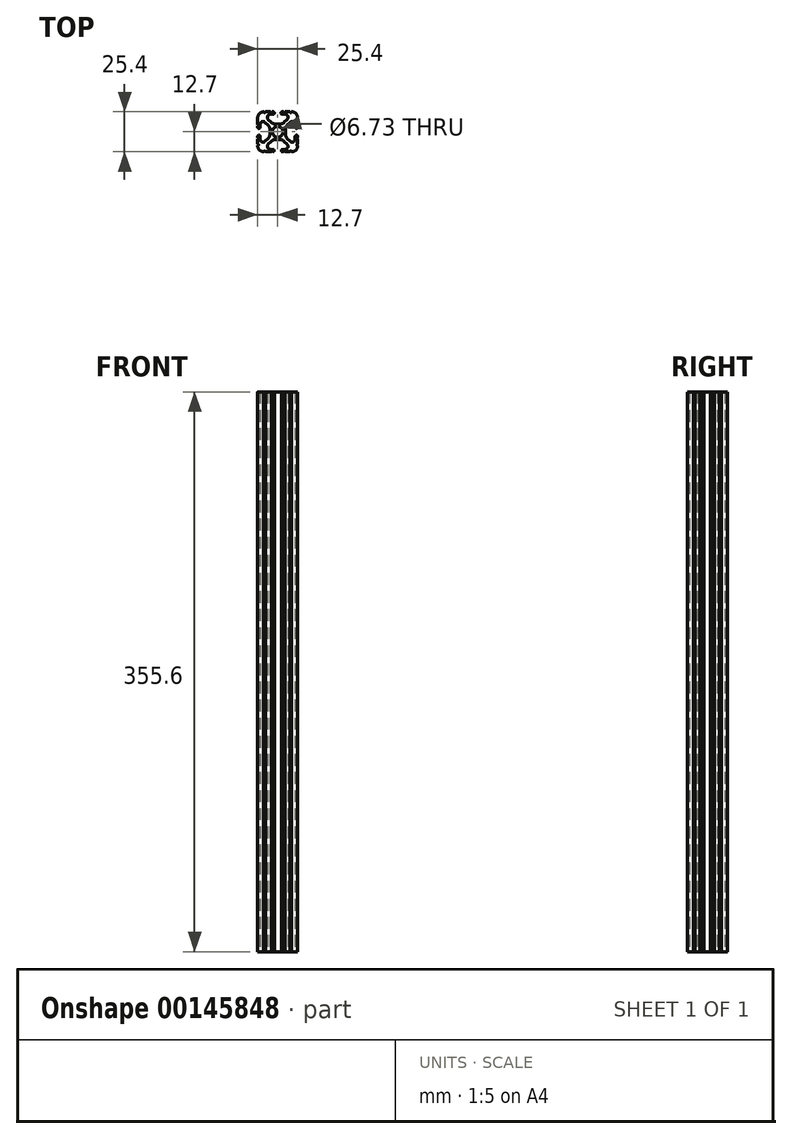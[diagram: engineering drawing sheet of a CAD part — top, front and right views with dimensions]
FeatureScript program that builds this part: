
annotation { "Feature Type Name" : "Feature", "Feature Type Description" : "" }
export const myFeature = defineFeature(function(context is Context, id is Id, definition is map)
    precondition{}
    {
        {
            var Q0;
            Q0=qCreatedBy(makeId("Top.planeOp"),FACE);
            var sketch = newSketch(context, id + "F0", { "sketchPlane" : qUnion([Q0])});
            skCircle(sketch, "E0", {"center": v(-12.7, 12.7) * mm, "radius": 3.36 * mm});
            skLineSegment(sketch, "E1.bottom", {"start": v(-11.24, 17.64) * mm, "end": v(-14.16, 17.64) * mm});
            skLineSegment(sketch, "E1.top", {"start": v(-11.24, 7.76) * mm, "end": v(-14.16, 7.76) * mm});
            skLineSegment(sketch, "E1.left", {"start": v(-7.76, 14.16) * mm, "end": v(-7.76, 11.24) * mm});
            skLineSegment(sketch, "E1.right", {"start": v(-17.64, 14.16) * mm, "end": v(-17.64, 11.24) * mm});
            skPoint(sketch, "E2.visualSharp", {"position": v(-25.4, 25.4) * mm});
            skPoint(sketch, "E3.visualSharp", {"position": v(0, 25.4) * mm});
            skPoint(sketch, "E4.visualSharp", {"position": v(0, 0) * mm});
            skPoint(sketch, "E5.visualSharp", {"position": v(-25.4, 0) * mm});
            skLineSegment(sketch, "E6.0", {"start": v(-18.7, 20.6) * mm, "end": v(-16.85, 18.76) * mm});
            skLineSegment(sketch, "E7.0", {"start": v(-20.6, 18.7) * mm, "end": v(-18.76, 16.85) * mm});
            skPoint(sketch, "E8.orphan", {"position": v(-23.85, 1.55) * mm});
            skPoint(sketch, "E9.orphan", {"position": v(-23.85, 23.85) * mm});
            skPoint(sketch, "E10.orphan", {"position": v(-1.55, 23.85) * mm});
            skPoint(sketch, "E11.orphan", {"position": v(-1.55, 1.55) * mm});
            skLineSegment(sketch, "E12", {"start": v(-8.55, 6.64) * mm, "end": v(-6.7, 4.8) * mm});
            skLineSegment(sketch, "E13.0", {"start": v(-18.7, 4.8) * mm, "end": v(-16.85, 6.64) * mm});
            skLineSegment(sketch, "E14.0", {"start": v(-20.6, 6.7) * mm, "end": v(-18.76, 8.55) * mm});
            skLineSegment(sketch, "E15.0", {"start": v(-8.55, 18.76) * mm, "end": v(-6.7, 20.6) * mm});
            skPoint(sketch, "E16.visualSharp", {"position": v(-23.85, 21.95) * mm});
            skArc(sketch, "E16.filletArc", {"start": v(-20.6, 18.7) * mm, "mid": v(-22.68, 19.1) * mm, "end": v(-23.85, 17.35) * mm});
            skPoint(sketch, "E17.visualSharp", {"position": v(-21.95, 23.85) * mm});
            skArc(sketch, "E17.filletArc", {"start": v(-17.35, 23.85) * mm, "mid": v(-19.1, 22.68) * mm, "end": v(-18.7, 20.6) * mm});
            skPoint(sketch, "E18.visualSharp", {"position": v(-5.34, 23.85) * mm});
            skLineSegment(sketch, "E19", {"start": v(-17.35, 23.85) * mm, "end": v(-15.58, 23.85) * mm});
            skLineSegment(sketch, "E20", {"start": v(-23.85, 17.35) * mm, "end": v(-23.85, 15.62) * mm});
            skLineSegment(sketch, "E21", {"start": v(-8.05, 1.55) * mm, "end": v(-9.78, 1.55) * mm});
            skArc(sketch, "E22.filletArc", {"start": v(-6.7, 20.6) * mm, "mid": v(-6.3, 22.68) * mm, "end": v(-8.05, 23.85) * mm});
            skPoint(sketch, "E23.visualSharp", {"position": v(-1.55, 3.45) * mm});
            skPoint(sketch, "E24.visualSharp", {"position": v(-3.45, 1.55) * mm});
            skArc(sketch, "E24.filletArc", {"start": v(-8.05, 1.55) * mm, "mid": v(-6.3, 2.73) * mm, "end": v(-6.7, 4.8) * mm});
            skArc(sketch, "E25.filletArc", {"start": v(-18.7, 4.8) * mm, "mid": v(-19.1, 2.73) * mm, "end": v(-17.35, 1.55) * mm});
            skArc(sketch, "E26.filletArc", {"start": v(-23.85, 8.05) * mm, "mid": v(-22.68, 6.3) * mm, "end": v(-20.6, 6.7) * mm});
            skLineSegment(sketch, "E27.bottom", {"start": v(-4.9, 0) * mm, "end": v(-8.05, 0) * mm});
            skLineSegment(sketch, "E27.top", {"start": v(-4.92, 25.4) * mm, "end": v(-8.05, 25.4) * mm});
            skLineSegment(sketch, "E27.left", {"start": v(0, 4.9) * mm, "end": v(0, 8.05) * mm});
            skLineSegment(sketch, "E27.right", {"start": v(-25.4, 4.9) * mm, "end": v(-25.4, 8.05) * mm});
            skArc(sketch, "E28.filletArc", {"start": v(-25.4, 3.81) * mm, "mid": v(-24.28, 1.12) * mm, "end": v(-21.59, 0) * mm});
            skArc(sketch, "E29.filletArc", {"start": v(-3.81, 0) * mm, "mid": v(-1.12, 1.12) * mm, "end": v(0, 3.8) * mm});
            skArc(sketch, "E30.filletArc", {"start": v(0, 21.59) * mm, "mid": v(-1.12, 24.28) * mm, "end": v(-3.8, 25.4) * mm});
            skArc(sketch, "E31.filletArc", {"start": v(-21.59, 25.4) * mm, "mid": v(-24.28, 24.28) * mm, "end": v(-25.4, 21.59) * mm});
            skPoint(sketch, "E32.newPointA", {"position": v(-17.64, 7.76) * mm});
            skArc(sketch, "E32.filletArc", {"start": v(-14.16, 7.76) * mm, "mid": v(-15.62, 7.47) * mm, "end": v(-16.85, 6.64) * mm});
            skPoint(sketch, "E33.newPointA", {"position": v(-7.76, 7.76) * mm});
            skArc(sketch, "E33.filletArc", {"start": v(-8.55, 6.64) * mm, "mid": v(-9.78, 7.47) * mm, "end": v(-11.24, 7.76) * mm});
            skArc(sketch, "E34.filletArc", {"start": v(-7.76, 11.24) * mm, "mid": v(-7.47, 9.78) * mm, "end": v(-6.64, 8.55) * mm});
            skArc(sketch, "E35.filletArc", {"start": v(-6.64, 16.85) * mm, "mid": v(-7.47, 15.62) * mm, "end": v(-7.76, 14.16) * mm});
            skPoint(sketch, "E36.newPointB", {"position": v(-7.76, 17.64) * mm});
            skArc(sketch, "E36.filletArc", {"start": v(-11.24, 17.64) * mm, "mid": v(-9.78, 17.93) * mm, "end": v(-8.55, 18.76) * mm});
            skPoint(sketch, "E37.newPointB", {"position": v(-17.64, 17.64) * mm});
            skArc(sketch, "E37.filletArc", {"start": v(-16.85, 18.76) * mm, "mid": v(-15.62, 17.93) * mm, "end": v(-14.16, 17.64) * mm});
            skArc(sketch, "E38.filletArc", {"start": v(-17.64, 14.16) * mm, "mid": v(-17.93, 15.62) * mm, "end": v(-18.76, 16.85) * mm});
            skArc(sketch, "E39.filletArc", {"start": v(-18.76, 8.55) * mm, "mid": v(-17.93, 9.78) * mm, "end": v(-17.64, 11.24) * mm});
            skLineSegment(sketch, "E40", {"start": v(-6.64, 8.55) * mm, "end": v(-4.8, 6.7) * mm});
            skPoint(sketch, "E41.visualSharp", {"position": v(-1.55, 21.95) * mm});
            skArc(sketch, "E42.filletArc", {"start": v(-4.8, 6.7) * mm, "mid": v(-2.73, 6.3) * mm, "end": v(-1.55, 8.05) * mm});
            skLineSegment(sketch, "E43", {"start": v(-1.55, 8.05) * mm, "end": v(-1.55, 9.78) * mm});
            skLineSegment(sketch, "E44", {"start": v(-6.64, 16.85) * mm, "end": v(-4.8, 18.7) * mm});
            skArc(sketch, "E45.filletArc", {"start": v(-1.55, 17.35) * mm, "mid": v(-2.73, 19.1) * mm, "end": v(-4.8, 18.7) * mm});
            skArc(sketch, "E46", {"start": v(-23.85, 9.78) * mm, "mid": v(-24.63, 10.56) * mm, "end": v(-25.4, 9.78) * mm});
            skArc(sketch, "E47", {"start": v(-25.4, 15.62) * mm, "mid": v(-24.63, 14.86) * mm, "end": v(-23.85, 15.62) * mm});
            skArc(sketch, "E48", {"start": v(-15.62, 23.85) * mm, "mid": v(-14.83, 24.63) * mm, "end": v(-15.62, 25.4) * mm});
            skArc(sketch, "E49", {"start": v(-9.78, 25.4) * mm, "mid": v(-10.6, 24.63) * mm, "end": v(-9.78, 23.85) * mm});
            skArc(sketch, "E50", {"start": v(-1.55, 15.62) * mm, "mid": v(-0.77, 14.88) * mm, "end": v(0, 15.62) * mm});
            skArc(sketch, "E51", {"start": v(0, 9.78) * mm, "mid": v(-0.77, 10.5) * mm, "end": v(-1.55, 9.78) * mm});
            skArc(sketch, "E52", {"start": v(-9.78, 1.55) * mm, "mid": v(-10.4, 0.77) * mm, "end": v(-9.78, 0) * mm});
            skArc(sketch, "E53", {"start": v(-15.62, 0) * mm, "mid": v(-14.85, 0.77) * mm, "end": v(-15.62, 1.55) * mm});
            skLineSegment(sketch, "E54.trimOffspring", {"start": v(-15.62, 1.55) * mm, "end": v(-17.35, 1.55) * mm});
            skLineSegment(sketch, "E55.trimOffspring", {"start": v(-16.7, 0) * mm, "end": v(-20.5, 0) * mm});
            skLineSegment(sketch, "E56.trimOffspring", {"start": v(-1.55, 15.62) * mm, "end": v(-1.55, 17.35) * mm});
            skLineSegment(sketch, "E57.trimOffspring", {"start": v(0, 15.62) * mm, "end": v(0, 16.26) * mm});
            skLineSegment(sketch, "E58.trimOffspring", {"start": v(-23.85, 9.78) * mm, "end": v(-23.85, 8.05) * mm});
            skLineSegment(sketch, "E59.trimOffspring", {"start": v(-25.4, 15.62) * mm, "end": v(-25.4, 16.26) * mm});
            skLineSegment(sketch, "E60.trimOffspring", {"start": v(-9.86, 23.85) * mm, "end": v(-8.05, 23.85) * mm});
            skLineSegment(sketch, "E61.trimOffspring", {"start": v(-15.58, 25.4) * mm, "end": v(-16.25, 25.4) * mm});
            skPoint(sketch, "E62.start.orphan", {"position": v(-15.62, 17.93) * mm});
            skPoint(sketch, "E63.start.orphan", {"position": v(-9.78, 17.93) * mm});
            skPoint(sketch, "E64.start.orphan", {"position": v(-7.47, 15.62) * mm});
            skPoint(sketch, "E65.start.orphan", {"position": v(-7.47, 9.78) * mm});
            skPoint(sketch, "E66.start.orphan", {"position": v(-17.93, 15.62) * mm});
            skPoint(sketch, "E67.start.orphan", {"position": v(-17.93, 9.78) * mm});
            skPoint(sketch, "E68.start.orphan", {"position": v(-9.78, 7.47) * mm});
            skPoint(sketch, "E69.start.orphan", {"position": v(-15.62, 7.47) * mm});
            skPoint(sketch, "E70.endSnap0", {"position": v(0, 18.6) * mm});
            skPoint(sketch, "E71.startSnap0", {"position": v(-1.55, 8.92) * mm});
            skArc(sketch, "E72", {"start": v(-4.92, 25.4) * mm, "mid": v(-4.37, 24.9) * mm, "end": v(-3.81, 25.4) * mm});
            skArc(sketch, "E73", {"start": v(-9.14, 25.4) * mm, "mid": v(-8.6, 24.86) * mm, "end": v(-8.05, 25.4) * mm});
            skArc(sketch, "E74", {"start": v(-17.35, 25.4) * mm, "mid": v(-16.8, 24.86) * mm, "end": v(-16.25, 25.4) * mm});
            skArc(sketch, "E75", {"start": v(-21.59, 25.4) * mm, "mid": v(-21.04, 24.85) * mm, "end": v(-20.49, 25.4) * mm});
            skLineSegment(sketch, "E76", {"start": v(-25.4, 21.59) * mm, "end": v(-25.4, 20.5) * mm});
            skArc(sketch, "E77", {"start": v(-25.4, 16.26) * mm, "mid": v(-24.84, 16.8) * mm, "end": v(-25.4, 17.35) * mm});
            skArc(sketch, "E78", {"start": v(-25.4, 8.05) * mm, "mid": v(-24.9, 8.6) * mm, "end": v(-25.4, 9.15) * mm});
            skArc(sketch, "E79", {"start": v(-25.4, 3.81) * mm, "mid": v(-24.85, 4.36) * mm, "end": v(-25.4, 4.9) * mm});
            skArc(sketch, "E80", {"start": v(-20.5, 0) * mm, "mid": v(-21.04, 0.55) * mm, "end": v(-21.59, 0) * mm});
            skArc(sketch, "E81", {"start": v(-15.62, 0) * mm, "mid": v(-16.16, 0.54) * mm, "end": v(-16.7, 0) * mm});
            skArc(sketch, "E82", {"start": v(-8.05, 0) * mm, "mid": v(-8.6, 0.55) * mm, "end": v(-9.15, 0) * mm});
            skArc(sketch, "E83", {"start": v(-3.81, 0) * mm, "mid": v(-4.35, 0.54) * mm, "end": v(-4.9, 0) * mm});
            skLineSegment(sketch, "E84.trimOffspring", {"start": v(-17.35, 25.4) * mm, "end": v(-20.49, 25.4) * mm});
            skLineSegment(sketch, "E85.trimOffspring", {"start": v(-25.4, 17.35) * mm, "end": v(-25.4, 21.59) * mm});
            skLineSegment(sketch, "E86.trimOffspring", {"start": v(-25.4, 9.15) * mm, "end": v(-25.4, 9.78) * mm});
            skLineSegment(sketch, "E87.trimOffspring", {"start": v(-9.15, 0) * mm, "end": v(-9.78, 0) * mm});
            skArc(sketch, "E88", {"start": v(0, 4.9) * mm, "mid": v(-0.54, 4.36) * mm, "end": v(0, 3.8) * mm});
            skArc(sketch, "E89", {"start": v(0, 9.15) * mm, "mid": v(-0.54, 8.6) * mm, "end": v(0, 8.05) * mm});
            skLineSegment(sketch, "E90.trimOffspring", {"start": v(0, 9.15) * mm, "end": v(0, 9.78) * mm});
            skArc(sketch, "E91", {"start": v(0, 21.59) * mm, "mid": v(-0.55, 21.04) * mm, "end": v(0, 20.5) * mm});
            skArc(sketch, "E92", {"start": v(0, 17.35) * mm, "mid": v(-0.55, 16.8) * mm, "end": v(0, 16.26) * mm});
            skLineSegment(sketch, "E93.trimOffspring", {"start": v(0, 17.35) * mm, "end": v(0, 20.5) * mm});
            skLineSegment(sketch, "E94.trimOffspring", {"start": v(-9.14, 25.4) * mm, "end": v(-9.86, 25.4) * mm});
            skSolve(sketch);
        }
        {
            var Q0;
            Q0=qSketchRegion(id+"F0",true);
            extrude(context, id + "F1", {"entities" : qUnion([Q0]), "depth" : 355.6 * mm});
        }
    });
